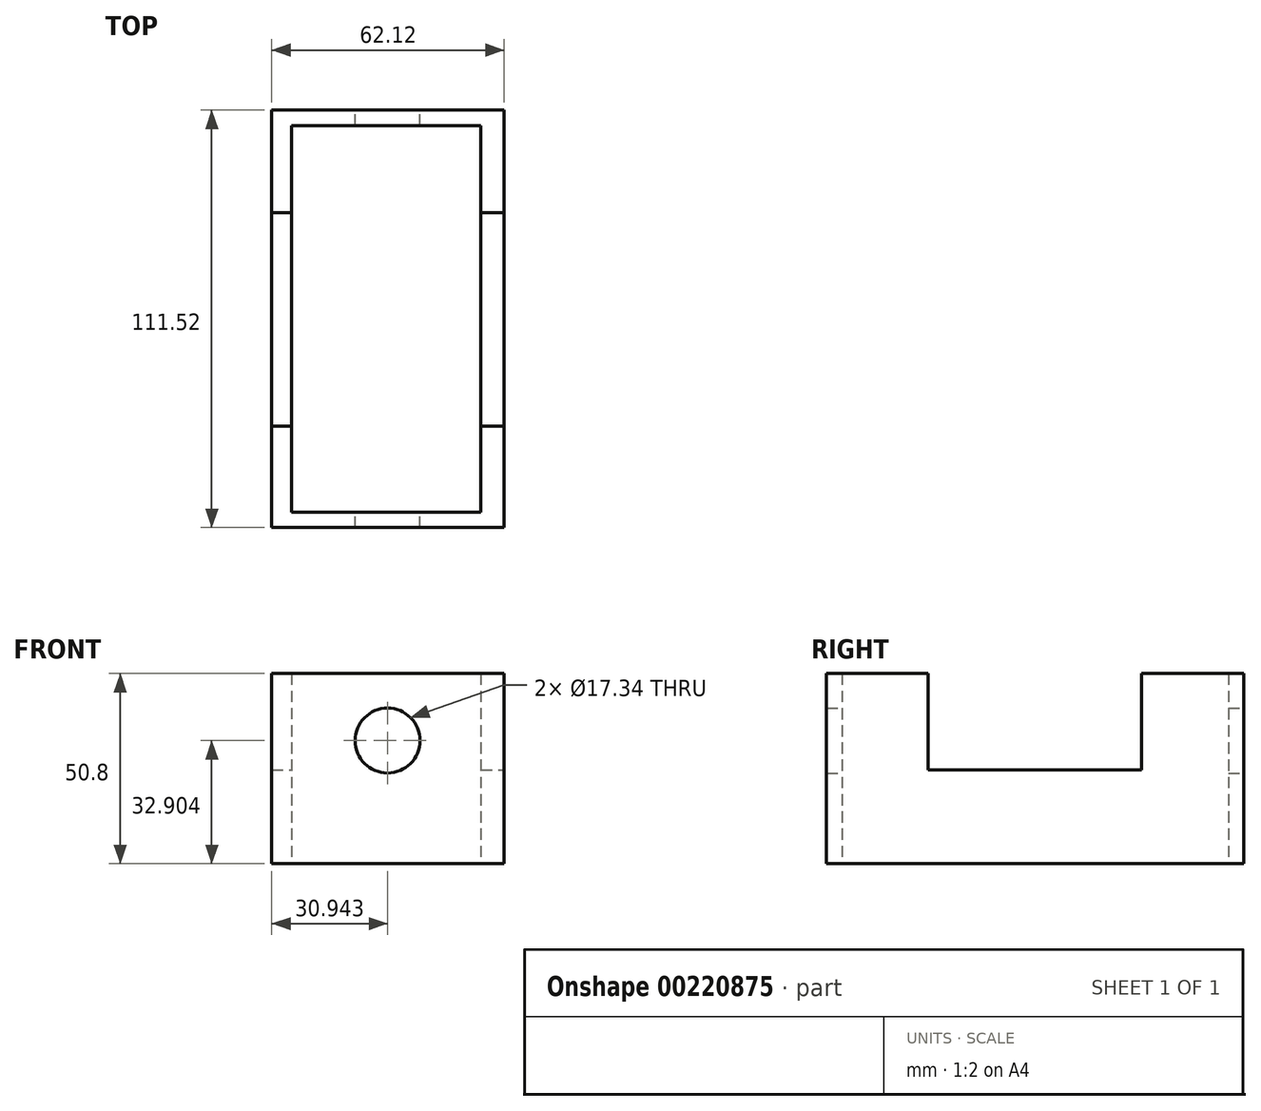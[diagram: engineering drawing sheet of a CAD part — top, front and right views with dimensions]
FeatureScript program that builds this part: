
annotation { "Feature Type Name" : "Feature", "Feature Type Description" : "" }
export const myFeature = defineFeature(function(context is Context, id is Id, definition is map)
    precondition{}
    {
        {
            var Q0;
            Q0=qCreatedBy(makeId("Top.planeOp"),FACE);
            var sketch = newSketch(context, id + "F0", { "sketchPlane" : qUnion([Q0])});
            skLineSegment(sketch, "E0.bottom", {"start": v(-32.79, 55.76) * mm, "end": v(29.33, 55.76) * mm});
            skLineSegment(sketch, "E0.top", {"start": v(-32.79, -55.76) * mm, "end": v(29.33, -55.76) * mm});
            skLineSegment(sketch, "E0.left", {"start": v(-32.79, 55.76) * mm, "end": v(-32.79, -55.76) * mm});
            skLineSegment(sketch, "E0.right", {"start": v(29.33, 55.76) * mm, "end": v(29.33, -55.76) * mm});
            skLineSegment(sketch, "E1.bottom", {"start": v(-27.48, 51.6) * mm, "end": v(23.1, 51.6) * mm});
            skLineSegment(sketch, "E1.top", {"start": v(-27.48, -51.6) * mm, "end": v(23.1, -51.6) * mm});
            skLineSegment(sketch, "E1.left", {"start": v(-27.48, 51.6) * mm, "end": v(-27.48, -51.6) * mm});
            skLineSegment(sketch, "E1.right", {"start": v(23.1, 51.6) * mm, "end": v(23.1, -51.6) * mm});
            skSolve(sketch);
        }
        {
            var Q0;
            Q0=makeQuery(id+"F0.imprint","IMPRINT",FACE,{"disambiguationData":[TD([[makeQuery(id+"F0.imprint","IMPRINT",EDGE,{"derivedFrom":sQuery(id+"F0.wireOp",EDGE,"E0.bottom")}),-1.0]])]});
            extrude(context, id + "F1", {"entities" : qUnion([Q0]), "depth" : 50.8 * mm});
        }
        {
            var Q0;
            Q0=makeQuery(id+"F1.opExtrude","SWEPT_FACE",FACE,{"disambiguationData":[OSD([sQuery(id+"F0.wireOp",EDGE,"E0.right")])]});
            var sketch = newSketch(context, id + "F2", { "sketchPlane" : qUnion([Q0])});
            skLineSegment(sketch, "E2.bottom", {"start": v(-28.63, 50.8) * mm, "end": v(28.4, 50.8) * mm});
            skLineSegment(sketch, "E2.top", {"start": v(-28.63, 25.05) * mm, "end": v(28.4, 25.05) * mm});
            skLineSegment(sketch, "E2.left", {"start": v(-28.63, 50.8) * mm, "end": v(-28.63, 25.05) * mm});
            skLineSegment(sketch, "E2.right", {"start": v(28.4, 50.8) * mm, "end": v(28.4, 25.05) * mm});
            skSolve(sketch);
        }
        {
            var Q0;
            Q0=makeQuery(id+"F2.imprint","IMPRINT",FACE,{"disambiguationData":[TD([[makeQuery(id+"F2.imprint","IMPRINT",EDGE,{"derivedFrom":sQuery(id+"F2.wireOp",EDGE,"E2.bottom")}),1.0]])]});
            extrude(context, id + "F3", {"entities" : qUnion([Q0]), "operationType" : NewBodyOperationType.REMOVE, "oppositeDirection" : true, "depth" : 254 * mm});
        }
        {
            var Q0;
            Q0=makeQuery(id+"F1.opExtrude","SWEPT_FACE",FACE,{"disambiguationData":[OSD([sQuery(id+"F0.wireOp",EDGE,"E0.bottom")])]});
            var sketch = newSketch(context, id + "F4", { "sketchPlane" : qUnion([Q0])});
            skCircle(sketch, "E3", {"center": v(1.85, 32.9) * mm, "radius": 8.67 * mm});
            skSolve(sketch);
        }
        {
            var Q0;
            Q0=makeQuery(id+"F4.imprint","IMPRINT",FACE,{"disambiguationData":[TD([[makeQuery(id+"F4.imprint","IMPRINT",EDGE,{"derivedFrom":sQuery(id+"F4.wireOp",EDGE,"E3")}),1.0]])]});
            extrude(context, id + "F5", {"entities" : qUnion([Q0]), "operationType" : NewBodyOperationType.REMOVE, "oppositeDirection" : true, "depth" : 381 * mm});
        }
    });
